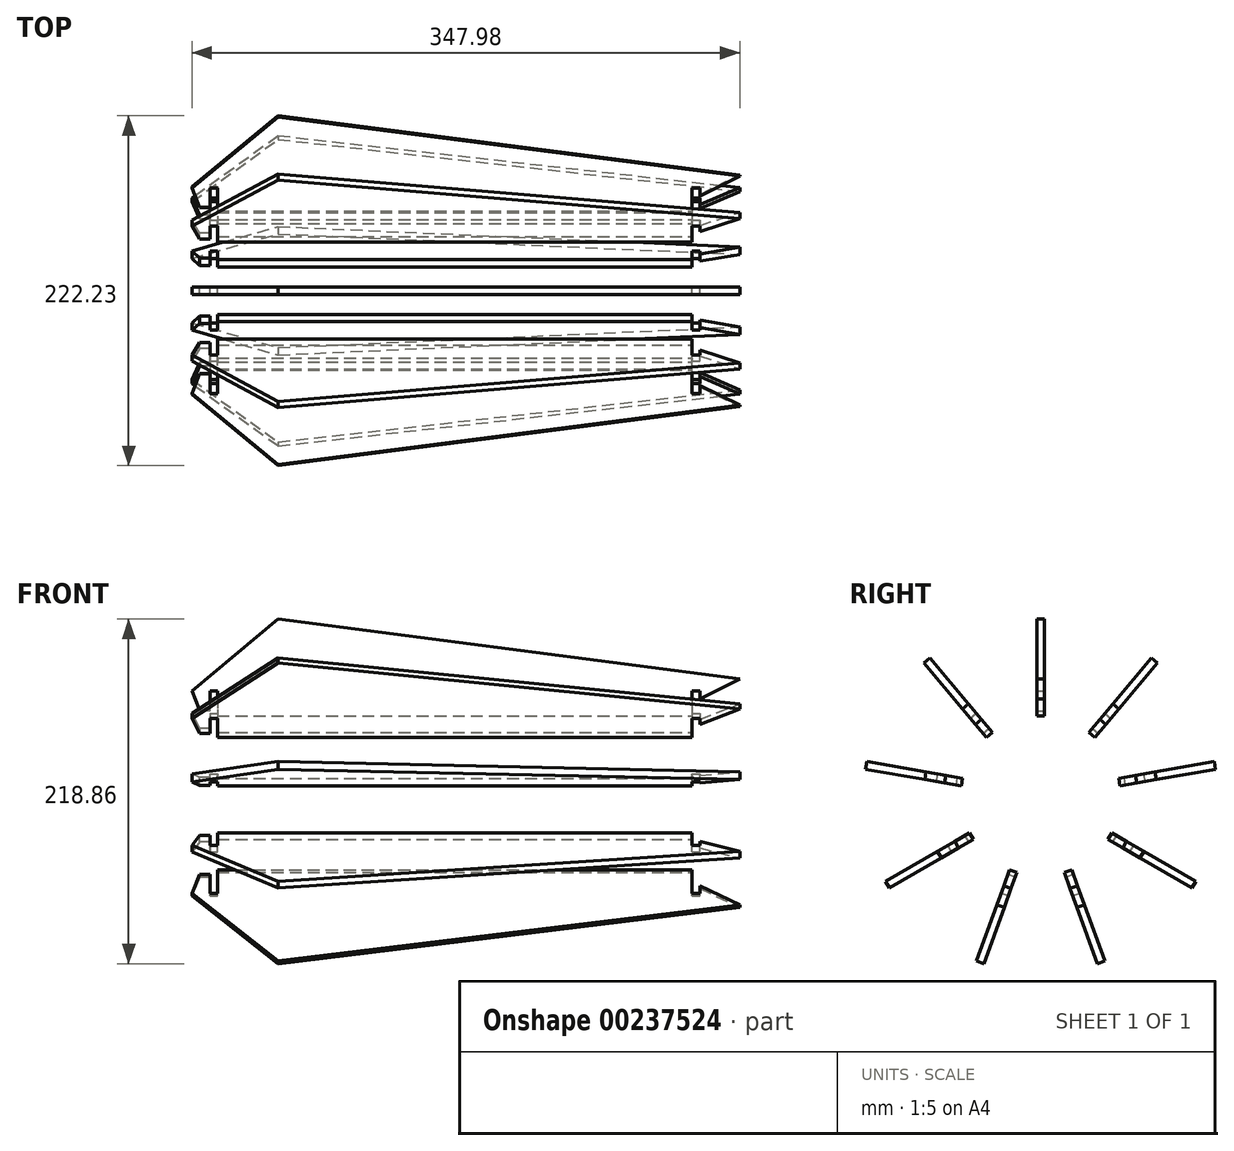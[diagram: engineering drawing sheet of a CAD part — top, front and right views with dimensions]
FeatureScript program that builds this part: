
annotation { "Feature Type Name" : "Feature", "Feature Type Description" : "" }
export const myFeature = defineFeature(function(context is Context, id is Id, definition is map)
    precondition{}
    {
        {
            var Q0;
            Q0=qCreatedBy(makeId("Front.planeOp"),FACE);
            var sketch = newSketch(context, id + "F0", { "sketchPlane" : qUnion([Q0])});
            skLineSegment(sketch, "E0", {"start": v(0, 0) * mm, "end": v(0, 12.7) * mm});
            skLineSegment(sketch, "E1", {"start": v(0, 12.7) * mm, "end": v(4.83, 12.7) * mm});
            skLineSegment(sketch, "E2", {"start": v(0, 0) * mm, "end": v(-6.35, 0) * mm});
            skLineSegment(sketch, "E3", {"start": v(-6.35, 0) * mm, "end": v(-11.43, 12.7) * mm});
            skLineSegment(sketch, "E4", {"start": v(-11.43, 12.7) * mm, "end": v(0, 22.23) * mm});
            skLineSegment(sketch, "E5", {"start": v(0, 22.23) * mm, "end": v(43.43, 58.42) * mm});
            skLineSegment(sketch, "E6", {"start": v(306.32, 12.7) * mm, "end": v(306.32, -3.18) * mm});
            skLineSegment(sketch, "E7", {"start": v(4.83, 12.7) * mm, "end": v(4.83, -3.18) * mm});
            skLineSegment(sketch, "E8", {"start": v(4.83, -3.18) * mm, "end": v(306.32, -3.18) * mm});
            skLineSegment(sketch, "E9", {"start": v(306.32, 12.7) * mm, "end": v(311.15, 12.7) * mm});
            skLineSegment(sketch, "E10", {"start": v(311.15, 12.7) * mm, "end": v(311.15, 7.62) * mm});
            skLineSegment(sketch, "E11", {"start": v(311.15, 7.62) * mm, "end": v(336.55, 20.32) * mm});
            skLineSegment(sketch, "E12", {"start": v(43.43, 58.42) * mm, "end": v(336.55, 20.32) * mm});
            skLineSegment(sketch, "E13", {"start": v(4.83, 12.7) * mm, "end": v(306.32, 12.7) * mm, "construction": true});
            skSolve(sketch);
        }
        {
            var Q0;
            Q0=makeQuery(id+"F0.imprint","IMPRINT",FACE,{"disambiguationData":[TD([[makeQuery(id+"F0.imprint","IMPRINT",EDGE,{"derivedFrom":sQuery(id+"F0.wireOp",EDGE,"E0")}),1.0]])]});
            extrude(context, id + "F1", {"entities" : qUnion([Q0]), "depth" : 4.95 * mm});
        }
        {
            var Q0;
            Q0=makeQuery(id+"F1.opExtrude","SWEPT_FACE",FACE,{"disambiguationData":[OSD([sQuery(id+"F0.wireOp",EDGE,"E7")])]});
            var sketch = newSketch(context, id + "F2", { "sketchPlane" : qUnion([Q0])});
            skPoint(sketch, "E14", {"position": v(2.48, -3.18) * mm});
            skCircle(sketch, "E15", {"center": v(2.48, -53.98) * mm, "radius": 50.8 * mm, "construction": true});
            skSolve(sketch);
        }
        {
            var Q0;
            Q0=makeQuery(id+"F1.opExtrude","CAP_FACE",FACE,{"disambiguationData":[OSD([sQuery(id+"F0.wireOp",EDGE,"E0"),sQuery(id+"F0.wireOp",EDGE,"E1"),sQuery(id+"F0.wireOp",EDGE,"E2"),sQuery(id+"F0.wireOp",EDGE,"E3"),sQuery(id+"F0.wireOp",EDGE,"E4"),sQuery(id+"F0.wireOp",EDGE,"E5"),sQuery(id+"F0.wireOp",EDGE,"E6"),sQuery(id+"F0.wireOp",EDGE,"E7"),sQuery(id+"F0.wireOp",EDGE,"E8"),sQuery(id+"F0.wireOp",EDGE,"E9"),sQuery(id+"F0.wireOp",EDGE,"E10"),sQuery(id+"F0.wireOp",EDGE,"E11"),sQuery(id+"F0.wireOp",EDGE,"E12")])],"isStart":false});
            var Q1;
            Q1=makeQuery(id+"F1.opExtrude","CAP_FACE",FACE,{"disambiguationData":[OSD([sQuery(id+"F0.wireOp",EDGE,"E0"),sQuery(id+"F0.wireOp",EDGE,"E1"),sQuery(id+"F0.wireOp",EDGE,"E2"),sQuery(id+"F0.wireOp",EDGE,"E3"),sQuery(id+"F0.wireOp",EDGE,"E4"),sQuery(id+"F0.wireOp",EDGE,"E5"),sQuery(id+"F0.wireOp",EDGE,"E6"),sQuery(id+"F0.wireOp",EDGE,"E7"),sQuery(id+"F0.wireOp",EDGE,"E8"),sQuery(id+"F0.wireOp",EDGE,"E9"),sQuery(id+"F0.wireOp",EDGE,"E10"),sQuery(id+"F0.wireOp",EDGE,"E11"),sQuery(id+"F0.wireOp",EDGE,"E12")])],"isStart":true});
            cPlane(context, id + "F3", {"entities" : qUnion([Q0, Q1]), "cplaneType" : CPlaneType.MID_PLANE, "offset" : 25.4 * mm, "width" : 152.4 * mm, "height" : 152.4 * mm});
        }
        {
            var Q0;
            Q0=makeQuery(id+"F1.opExtrude","SWEPT_BODY",BODY,{"disambiguationData":[OSD([sQuery(id+"F0.wireOp",EDGE,"E0"),sQuery(id+"F0.wireOp",EDGE,"E1"),sQuery(id+"F0.wireOp",EDGE,"E2"),sQuery(id+"F0.wireOp",EDGE,"E3"),sQuery(id+"F0.wireOp",EDGE,"E4"),sQuery(id+"F0.wireOp",EDGE,"E5"),sQuery(id+"F0.wireOp",EDGE,"E6"),sQuery(id+"F0.wireOp",EDGE,"E7"),sQuery(id+"F0.wireOp",EDGE,"E8"),sQuery(id+"F0.wireOp",EDGE,"E9"),sQuery(id+"F0.wireOp",EDGE,"E10"),sQuery(id+"F0.wireOp",EDGE,"E11"),sQuery(id+"F0.wireOp",EDGE,"E12")])]});
            var Q1;
            Q1=sQuery(id+"F2.wireOp",EDGE,"E15");
            circularPattern(context, id + "F4", {"entities" : qUnion([Q0]), "axis" : qUnion([Q1]), "angle" : 360 * degree, "instanceCount" : 9, "equalSpace" : true});
        }
    });
